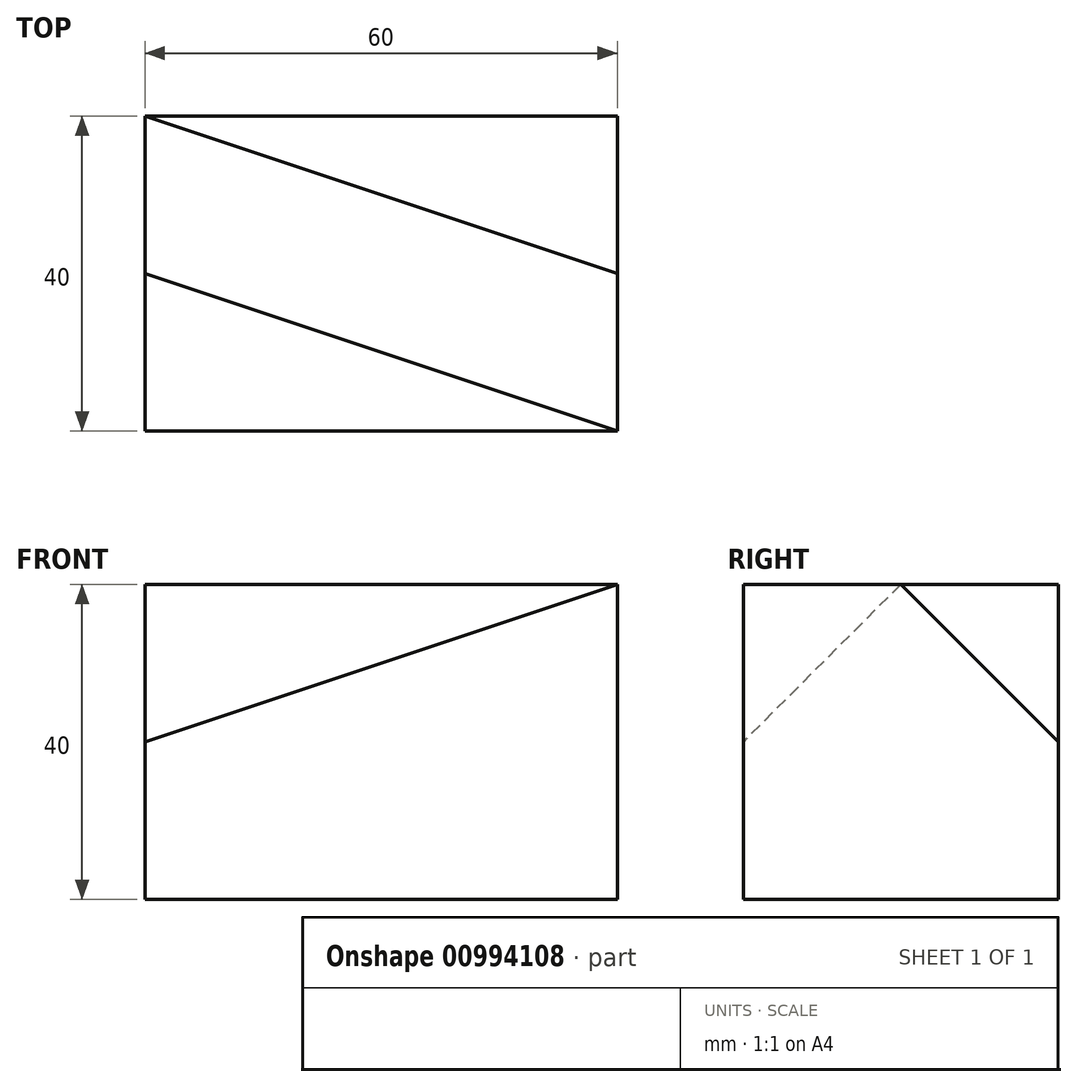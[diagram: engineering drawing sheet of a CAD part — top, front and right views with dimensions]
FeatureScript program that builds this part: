
annotation { "Feature Type Name" : "Feature", "Feature Type Description" : "" }
export const myFeature = defineFeature(function(context is Context, id is Id, definition is map)
    precondition{}
    {
        {
            var Q0;
            Q0=qCreatedBy(makeId("Top.planeOp"),FACE);
            var sketch = newSketch(context, id + "F0", { "sketchPlane" : qUnion([Q0])});
            skLineSegment(sketch, "E0.bottom", {"start": v(0, 0) * mm, "end": v(60, 0) * mm});
            skLineSegment(sketch, "E0.top", {"start": v(0, 40) * mm, "end": v(60, 40) * mm});
            skLineSegment(sketch, "E0.left", {"start": v(0, 0) * mm, "end": v(0, 40) * mm});
            skLineSegment(sketch, "E0.right", {"start": v(60, 0) * mm, "end": v(60, 40) * mm});
            skSolve(sketch);
        }
        {
            var Q0;
            Q0=makeQuery(id+"F0.imprint","IMPRINT",FACE,{"disambiguationData":[TD([[makeQuery(id+"F0.imprint","IMPRINT",EDGE,{"derivedFrom":sQuery(id+"F0.wireOp",EDGE,"E0.bottom")}),1.0]])]});
            extrude(context, id + "F1", {"entities" : qUnion([Q0]), "depth" : 40 * mm, "offsetDistance" : 25 * mm});
        }
        {
            var Q0;
            Q0=makeQuery(id+"F1.opExtrude","CAP_FACE",FACE,{"disambiguationData":[OSD([sQuery(id+"F0.wireOp",EDGE,"E0.bottom"),sQuery(id+"F0.wireOp",EDGE,"E0.top"),sQuery(id+"F0.wireOp",EDGE,"E0.left"),sQuery(id+"F0.wireOp",EDGE,"E0.right")])],"isStart":false});
            var sketch = newSketch(context, id + "F2", { "sketchPlane" : qUnion([Q0])});
            skLineSegment(sketch, "E1", {"start": v(0, 20) * mm, "end": v(60, 0) * mm});
            skLineSegment(sketch, "E2", {"start": v(0, 40) * mm, "end": v(60, 20) * mm});
            skSolve(sketch);
        }
        {
            var Q0;
            Q0=sQuery(id+"F2.wireOp",VERTEX,"E1.start");
            var Q1;
            Q1=sQuery(id+"F2.wireOp",EDGE,"E1");
            cPlane(context, id + "F3", {"entities" : qUnion([Q0, Q1]), "cplaneType" : CPlaneType.LINE_POINT, "offset" : 25 * mm, "width" : 150 * mm, "height" : 150 * mm});
        }
        {
            var Q0;
            Q0=qCreatedBy(id+"F3.planeOp",FACE);
            var sketch = newSketch(context, id + "F4", { "sketchPlane" : qUnion([Q0])});
            skLineSegment(sketch, "E3.0", {"start": v(0, 40) * mm, "end": v(37.95, 40) * mm});
            skLineSegment(sketch, "E4.0", {"start": v(0, 40) * mm, "end": v(0, 0) * mm});
            skLineSegment(sketch, "E5", {"start": v(18.97, 40) * mm, "end": v(0, 20) * mm});
            skSolve(sketch);
        }
        {
            var Q0;
            {var subQ3=sQuery(id+"F4.wireOp",EDGE,"E5");Q0=makeQuery(id+"F4.imprint","IMPRINT",FACE,{"disambiguationData":[TD([[makeQuery(id+"F4.imprint","IMPRINT",EDGE,{"derivedFrom":subQ3}),-1.0]])]});}
            extrude(context, id + "F5", {"entities" : qUnion([Q0]), "operationType" : NewBodyOperationType.REMOVE, "endBound" : BoundingType.THROUGH_ALL, "depth" : 25 * mm, "offsetDistance" : 25 * mm});
        }
        {
            var Q0;
            Q0=sQuery(id+"F2.wireOp",EDGE,"E2");
            var Q1;
            Q1=sQuery(id+"F2.wireOp",VERTEX,"E2.end");
            cPlane(context, id + "F6", {"entities" : qUnion([Q0, Q1]), "cplaneType" : CPlaneType.LINE_POINT, "offset" : 25 * mm, "width" : 150 * mm, "height" : 150 * mm});
        }
        {
            var Q0;
            Q0=qCreatedBy(id+"F6.planeOp",FACE);
            var sketch = newSketch(context, id + "F7", { "sketchPlane" : qUnion([Q0])});
            skLineSegment(sketch, "E6.0", {"start": v(18.97, 40) * mm, "end": v(56.92, 40) * mm});
            skLineSegment(sketch, "E7.0", {"start": v(56.92, 40) * mm, "end": v(56.92, 0) * mm});
            skLineSegment(sketch, "E8", {"start": v(37.95, 40) * mm, "end": v(56.92, 20) * mm});
            skSolve(sketch);
        }
        {
            var Q0;
            {var subQ3=sQuery(id+"F7.wireOp",EDGE,"E8");Q0=makeQuery(id+"F7.imprint","IMPRINT",FACE,{"disambiguationData":[TD([[makeQuery(id+"F7.imprint","IMPRINT",EDGE,{"derivedFrom":subQ3}),1.0]])]});}
            extrude(context, id + "F8", {"entities" : qUnion([Q0]), "operationType" : NewBodyOperationType.REMOVE, "endBound" : BoundingType.THROUGH_ALL, "oppositeDirection" : true, "depth" : 25 * mm, "offsetDistance" : 25 * mm});
        }
    });
